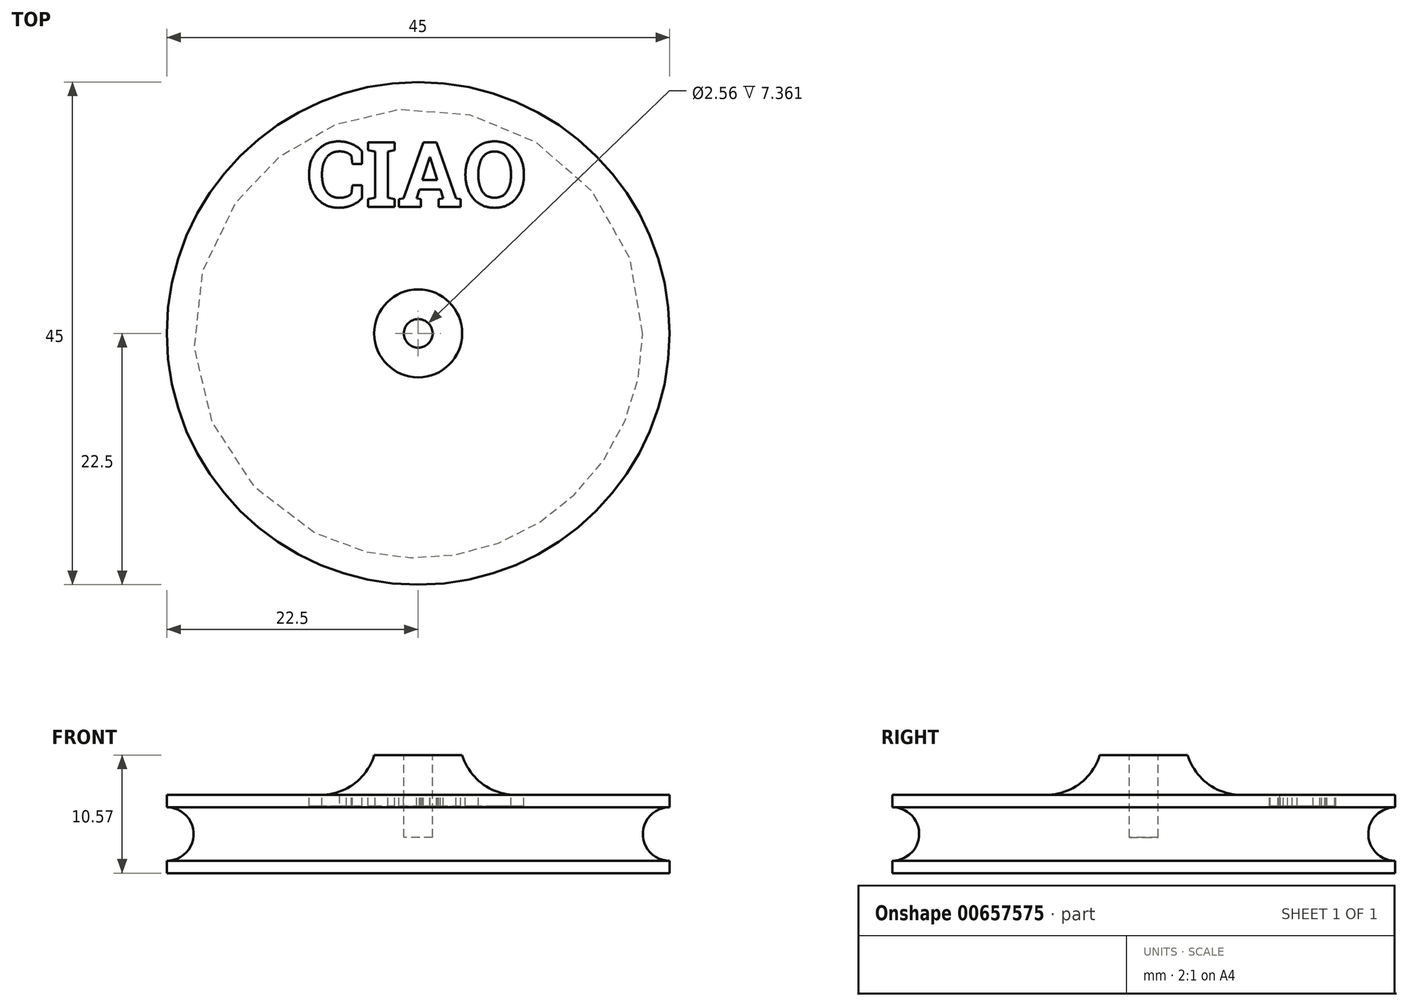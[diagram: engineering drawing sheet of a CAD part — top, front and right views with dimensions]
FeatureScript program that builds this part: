
annotation { "Feature Type Name" : "Feature", "Feature Type Description" : "" }
export const myFeature = defineFeature(function(context is Context, id is Id, definition is map)
    precondition{}
    {
        {
            var Q0;
            Q0=qCreatedBy(makeId("Front.planeOp"),FACE);
            var sketch = newSketch(context, id + "F0", { "sketchPlane" : qUnion([Q0])});
            skLineSegment(sketch, "E0", {"start": v(0, 0) * mm, "end": v(22.5, 0) * mm});
            skLineSegment(sketch, "E1", {"start": v(22.5, 0) * mm, "end": v(22.5, 7) * mm});
            skLineSegment(sketch, "E2", {"start": v(22.5, 7) * mm, "end": v(3.94, 7) * mm});
            skLineSegment(sketch, "E3", {"start": v(3.94, 7) * mm, "end": v(3.94, 10.57) * mm});
            skLineSegment(sketch, "E4", {"start": v(3.94, 10.57) * mm, "end": v(0, 10.57) * mm});
            skLineSegment(sketch, "E5", {"start": v(0, 10.57) * mm, "end": v(0, 0) * mm});
            skLineSegment(sketch, "E6", {"start": v(0, 3.2) * mm, "end": v(1.28, 3.2) * mm});
            skLineSegment(sketch, "E7", {"start": v(1.28, 3.2) * mm, "end": v(1.28, 10.57) * mm});
            skCircle(sketch, "E8", {"center": v(22.5, 3.5) * mm, "radius": 2.4 * mm});
            skSolve(sketch);
        }
        {
            var Q0;
            {var subQ4=sQuery(id+"F0.wireOp",EDGE,"E0");Q0=makeQuery(id+"F0.imprint","IMPRINT",FACE,{"disambiguationData":[TD([[makeQuery(id+"F0.imprint","IMPRINT",EDGE,{"derivedFrom":subQ4}),1.0]])]});}
            var Q1;
            Q1=sQuery(id+"F0.wireOp",EDGE,"E5");
            revolve(context, id + "F1", {"entities" : qUnion([Q0]), "axis" : qUnion([Q1]), "revolveType" : RevolveType.FULL});
        }
        {
            var Q0;
            Q0=makeQuery(id+"F1.opRevolve","SWEPT_EDGE",EDGE,{"disambiguationData":[OSD([sQuery(id+"F0.wireOp",EDGE,"E2"),sQuery(id+"F0.wireOp",EDGE,"E3")])]});
            fillet(context, id + "F2", {"entities" : qUnion([Q0]), "radius" : 5 * mm, "tangentPropagation" : true, "allowEdgeOverflow" : false});
        }
        {
            var Q0;
            Q0=makeQuery(id+"F1.opRevolve","SWEPT_FACE",FACE,{"disambiguationData":[OSD([sQuery(id+"F0.wireOp",EDGE,"E2")])]});
            var sketch = newSketch(context, id + "F3", { "sketchPlane" : qUnion([Q0])});
            skText(sketch, "E9", { "text": "CIAO", "fontName": "RobotoSlab-Bold.ttf"});
            const initialGuessF3  = {"E9": [-0.00997, 0.01133, 1, 0, 0.00585]};
            skSetInitialGuess(sketch, initialGuessF3);
            skSolve(sketch);
        }
        {
            var Q0;
            Q0=makeQuery(id+"F3.imprint","IMPRINT",FACE,{"disambiguationData":[TD([[makeQuery(id+"F3.imprint","IMPRINT",EDGE,{"derivedFrom":sQuery(id+"F3.wireOp",EDGE,"E9.sketch_text.stroke-0")}),-1.0]])]});
            var Q1;
            Q1=makeQuery(id+"F3.imprint","IMPRINT",FACE,{"disambiguationData":[TD([[makeQuery(id+"F3.imprint","IMPRINT",EDGE,{"derivedFrom":sQuery(id+"F3.wireOp",EDGE,"E9.sketch_text.stroke-24")}),-1.0]])]});
            var Q2;
            Q2=makeQuery(id+"F3.imprint","IMPRINT",FACE,{"disambiguationData":[TD([[makeQuery(id+"F3.imprint","IMPRINT",EDGE,{"derivedFrom":sQuery(id+"F3.wireOp",EDGE,"E9.sketch_text.stroke-56")}),-1.0]])]});
            var Q3;
            Q3=makeQuery(id+"F3.imprint","IMPRINT",FACE,{"disambiguationData":[TD([[makeQuery(id+"F3.imprint","IMPRINT",EDGE,{"derivedFrom":sQuery(id+"F3.wireOp",EDGE,"E9.sketch_text.stroke-36")}),-1.0]])]});
            extrude(context, id + "F4", {"entities" : qUnion([Q0, Q1, Q2, Q3]), "operationType" : NewBodyOperationType.REMOVE, "oppositeDirection" : true, "depth" : 1 * mm, "offsetDistance" : 25 * mm});
        }
    });
